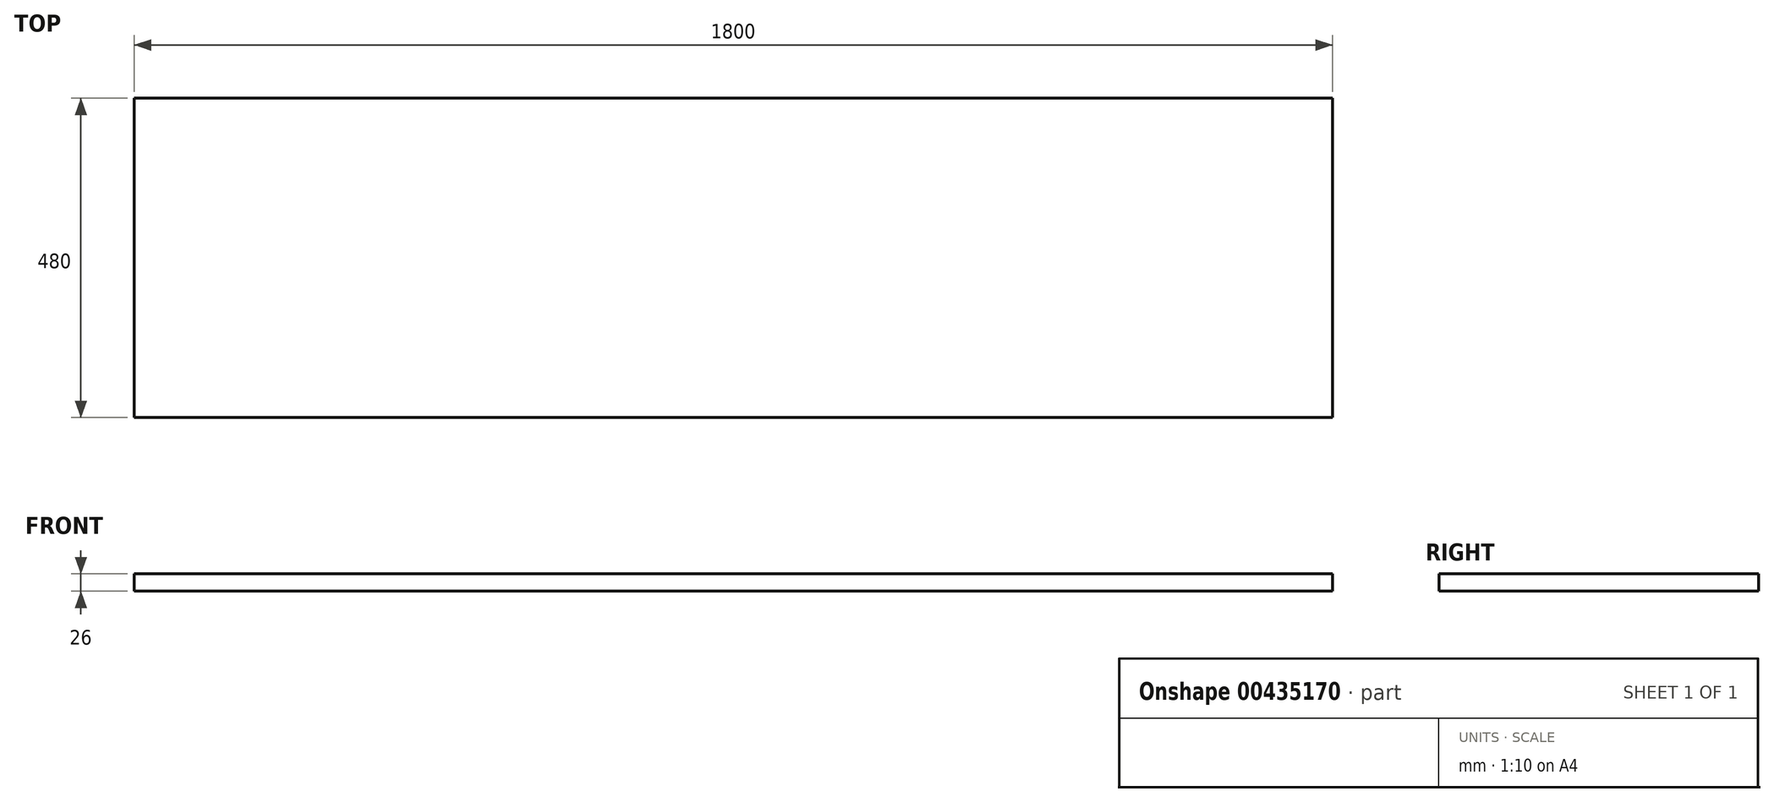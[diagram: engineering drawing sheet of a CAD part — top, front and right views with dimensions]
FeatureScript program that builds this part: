
annotation { "Feature Type Name" : "Feature", "Feature Type Description" : "" }
export const myFeature = defineFeature(function(context is Context, id is Id, definition is map)
    precondition{}
    {
        {
            var Q0;
            Q0=qCreatedBy(makeId("Top.planeOp"),FACE);
            var sketch = newSketch(context, id + "F0", { "sketchPlane" : qUnion([Q0])});
            skLineSegment(sketch, "E0.bottom", {"start": v(0, 0) * mm, "end": v(1800, 0) * mm});
            skLineSegment(sketch, "E0.top", {"start": v(0, 480) * mm, "end": v(1800, 480) * mm});
            skLineSegment(sketch, "E0.left", {"start": v(0, 0) * mm, "end": v(0, 480) * mm});
            skLineSegment(sketch, "E0.right", {"start": v(1800, 0) * mm, "end": v(1800, 480) * mm});
            skSolve(sketch);
        }
        {
            var Q0;
            Q0 = qSketchRegion(id + "F0", true);
            extrude(context, id + "F1", {"entities" : qUnion([Q0]), "depth" : 26 * mm});
        }
    });
